# Revit family: Haworth_ComposeStorage_Supports
name_source: partatom
category: Furniture Systems
revit_build: Autodesk Revit 2018 (Build: 20170223_1515(x64)
units: mm (PartAtom-declared; Revit-internal decimal feet)

## family parameters
Always vertical = Yes
Cut with Voids When Loaded = No
OmniClass Number = 23.40.70.14.64.21
OmniClass Title = Systems Furniture
Part Type = Normal
Room Calculation Point = No
Round Connector Dimension = Use Diameter
Shared = No
Work Plane-Based = No

## types (1)
- 28h 18w
    Actual Depth = 18"
    Actual Height = 28"
    Actual Width = 1"
    Base Finish = Haworth _ Wood _ Undecided _ Storage
    Custom Size = Yes
    Depth = 18"
    Description = Haworth - Compose Storage Supports
    Height = 28"
    Manufacturer = Haworth
    Model = ZxFS
    Revision Number = 4
    Size = Verify Final Dim. w/ Haworth
    Sustainability Info = http://media.haworth.com
    URL = www.haworth.com
    URL - Product = http://www.haworth.com
    Warranty = http://www.haworth.com
    Width = 1"

## geometry (parser evidence)
native form markers: Sweep x2
no freeform markers — native parametric forms only
